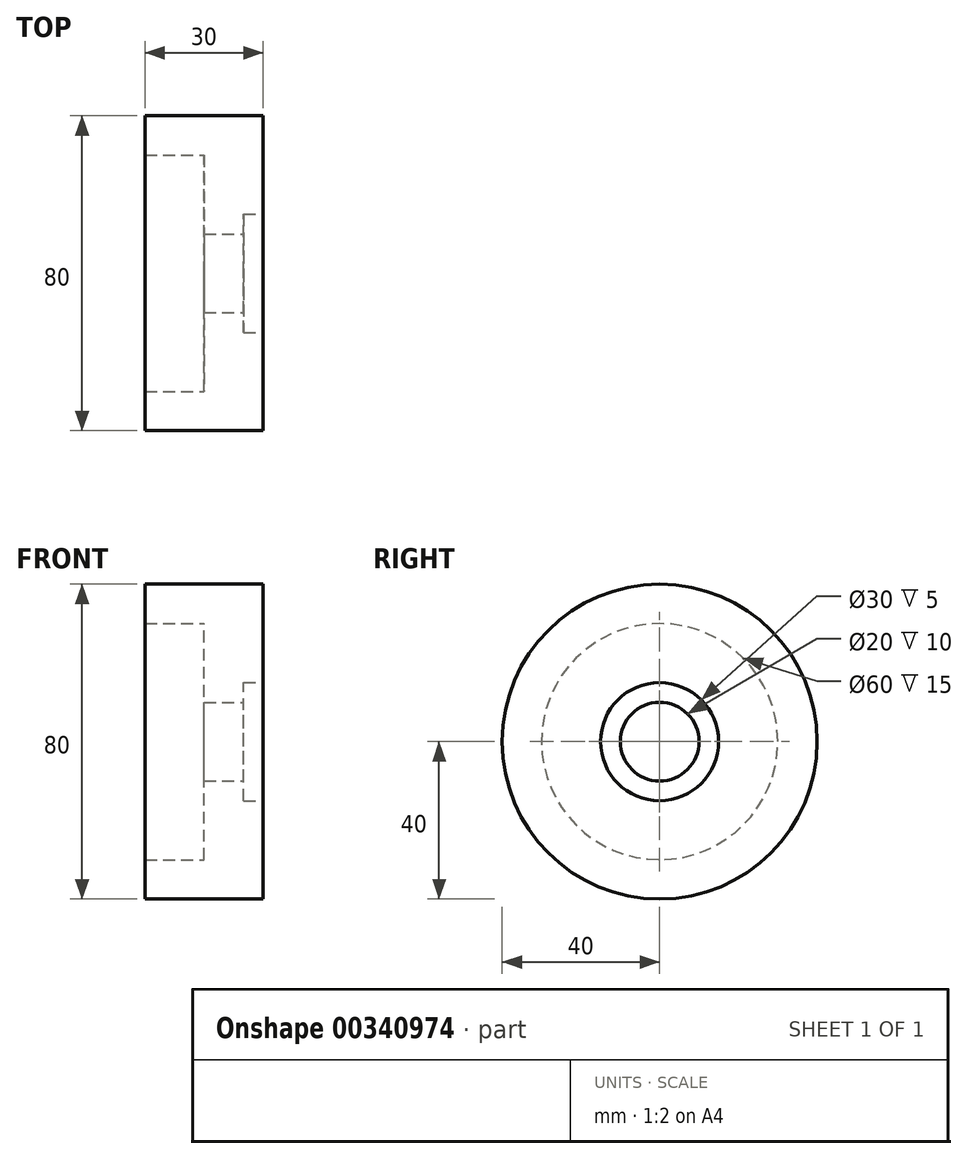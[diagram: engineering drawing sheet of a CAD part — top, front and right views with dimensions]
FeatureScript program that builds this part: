
annotation { "Feature Type Name" : "Feature", "Feature Type Description" : "" }
export const myFeature = defineFeature(function(context is Context, id is Id, definition is map)
    precondition{}
    {
        {
            var Q0;
            Q0=qCreatedBy(makeId("Front.planeOp"),FACE);
            var sketch = newSketch(context, id + "F0", { "sketchPlane" : qUnion([Q0])});
            skLineSegment(sketch, "E0", {"start": v(-30, -40) * mm, "end": v(0, -40) * mm});
            skLineSegment(sketch, "E1", {"start": v(-15, -30) * mm, "end": v(-30, -30) * mm});
            skLineSegment(sketch, "E2", {"start": v(-15, -10) * mm, "end": v(-5, -10) * mm});
            skLineSegment(sketch, "E3", {"start": v(0, -15) * mm, "end": v(-5, -15) * mm});
            skLineSegment(sketch, "E4", {"start": v(-5, -15) * mm, "end": v(-5, -10) * mm});
            skLineSegment(sketch, "E5.trimOffspring", {"start": v(-30, -30) * mm, "end": v(-30, -40) * mm});
            skLineSegment(sketch, "E6.MirrorCS", {"start": v(0, -15) * mm, "end": v(0, -40) * mm});
            skLineSegment(sketch, "E7.trimOffspring", {"start": v(-15, -10) * mm, "end": v(-15, -30) * mm});
            skPoint(sketch, "E8.end.orphan", {"position": v(-30, 40) * mm});
            skLineSegment(sketch, "E9", {"start": v(19.2, 0) * mm, "end": v(-38.23, 0) * mm, "construction": true});
            skSolve(sketch);
        }
        {
            var Q0;
            Q0=makeQuery(id+"F0.imprint","IMPRINT",FACE,{"disambiguationData":[TD([[makeQuery(id+"F0.imprint","IMPRINT",EDGE,{"derivedFrom":sQuery(id+"F0.wireOp",EDGE,"E0")}),1.0]])]});
            var Q1;
            Q1=sQuery(id+"F0.wireOp",EDGE,"E9");
            revolve(context, id + "F1", {"entities" : qUnion([Q0]), "axis" : qUnion([Q1]), "revolveType" : RevolveType.FULL});
        }
    });
